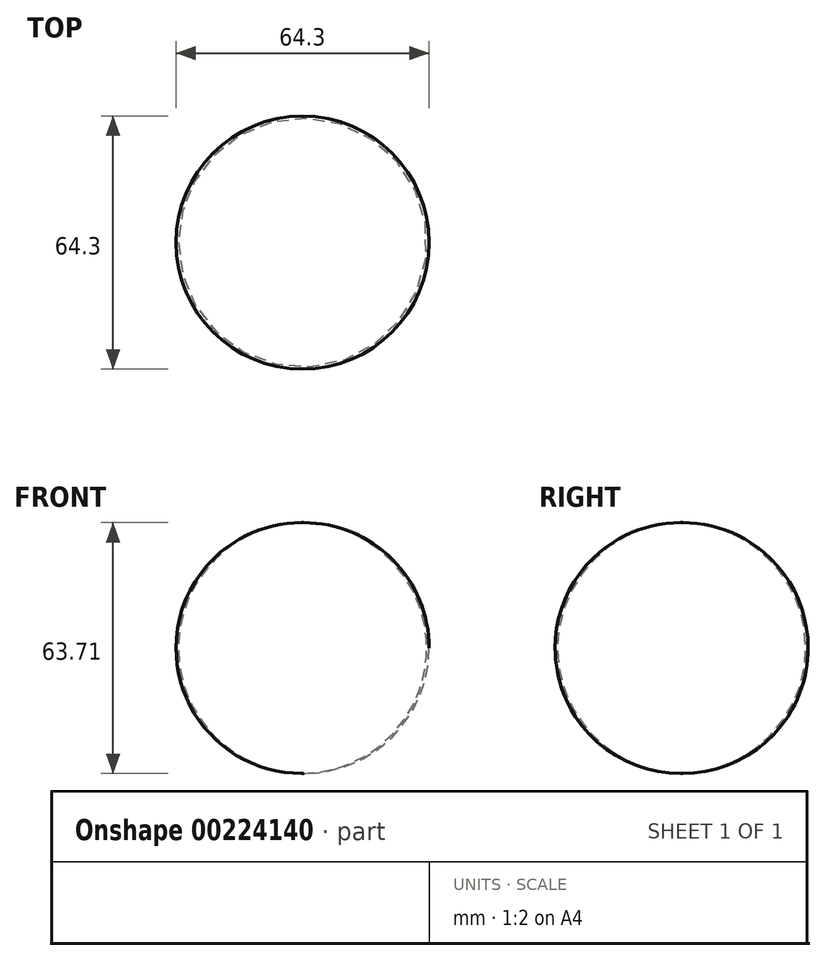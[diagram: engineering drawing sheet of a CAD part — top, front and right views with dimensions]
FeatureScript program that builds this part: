
annotation { "Feature Type Name" : "Feature", "Feature Type Description" : "" }
export const myFeature = defineFeature(function(context is Context, id is Id, definition is map)
    precondition{}
    {
        {
            var Q0;
            Q0=qCreatedBy(makeId("Front.planeOp"),FACE);
            var sketch = newSketch(context, id + "F0", { "sketchPlane" : qUnion([Q0])});
            skCircle(sketch, "E0", {"center": v(-0.3, -0.15) * mm, "radius": 31.85 * mm});
            skLineSegment(sketch, "E1", {"start": v(0, 31.7) * mm, "end": v(0, -32) * mm});
            skSolve(sketch);
        }
        {
            var Q0;
            {var subQ0=sQuery(id+"F0.wireOp",EDGE,"E1");Q0=makeQuery(id+"F0.imprint","IMPRINT",FACE,{"disambiguationData":[TD([[makeQuery(id+"F0.imprint","IMPRINT",EDGE,{"derivedFrom":subQ0}),1.0]])]});}
            var Q1;
            Q1=sQuery(id+"F0.wireOp",EDGE,"E1");
            revolve(context, id + "F1", {"entities" : qUnion([Q0]), "axis" : qUnion([Q1]), "revolveType" : RevolveType.FULL});
        }
    });
